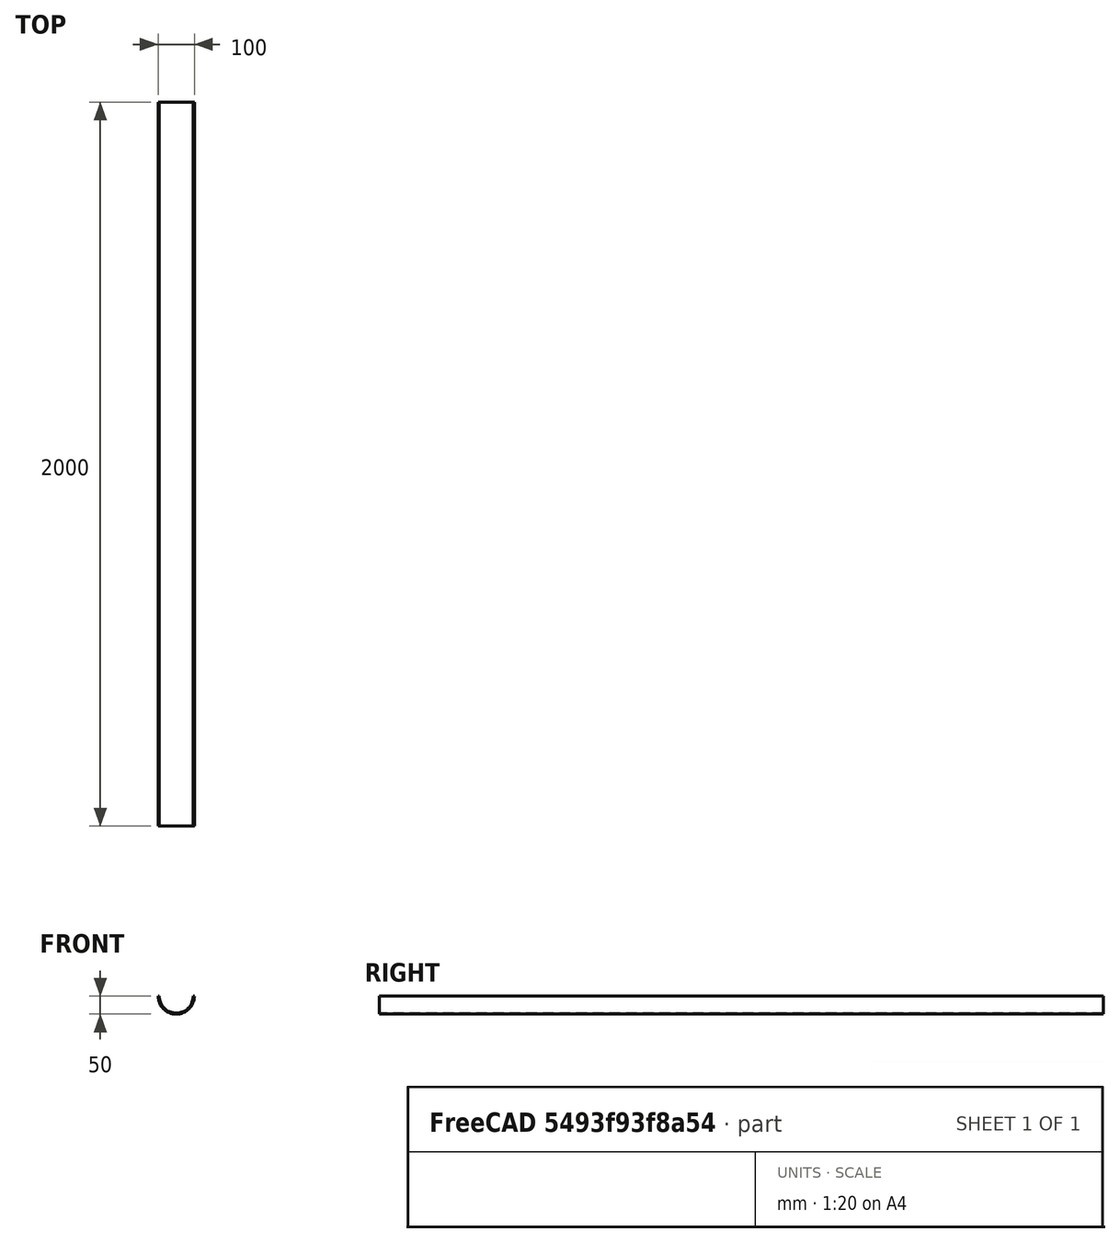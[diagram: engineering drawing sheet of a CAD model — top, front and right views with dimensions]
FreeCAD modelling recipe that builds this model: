
FCSTD DOCUMENT  (FreeCAD 0.15R4671 (Git))
Label: Demi tube sous miroir
License: All rights reserved
LicenseURL: http://en.wikipedia.org/wiki/All_rights_reserved
objects: Sketcher::SketchObject×1, Part::Extrusion×1
note: 2 computed .brp shape members not serialized (recipe doc carries the construction recipe); baked Part::Feature solids carry a one-line shape summary decoded from their .brp

FEATURE [Sketcher::SketchObject] Sketch
  Placement = pos=(0,0,0) rot=(-1,0,0;4.71239rad)
  sketch-geometry (4):
    g0: LineSegment StartX=-50 StartY=0 StartZ=0 EndX=-47 EndY=0 EndZ=0
    g1: LineSegment StartX=47 StartY=0 StartZ=0 EndX=50 EndY=0 EndZ=0
    g2: ArcOfCircle CenterX=0 CenterY=0 CenterZ=0 NormalX=0 NormalY=0 NormalZ=1 Radius=47 StartAngle=3.14159 EndAngle=6.28319
    g3: ArcOfCircle CenterX=0 CenterY=0 CenterZ=0 NormalX=0 NormalY=0 NormalZ=1 Radius=50 StartAngle=3.14159 EndAngle=6.28319
  constraints (13):
    c: Horizontal(g0)
    c: PointOnObject(g1,g-1)
    c: Horizontal(g1)
    c: Coincident(g2,g-1)
    c: PointOnObject(g2,g-1)
    c: Coincident(g3,g-1)
    c: Coincident(g3,g1)
    c: PointOnObject(g3,g-1)
    c: Coincident(g0,g3)
    c: Coincident(g0,g2)
    c: Distance(g0,g1) = 100
    c: Distance(g0,g0) = 3
    c: Coincident(g1,g2)
FEATURE [Part::Extrusion] Extrude001
  Base = -> Sketch
  Dir = (0,2000,0)
  Solid = true
